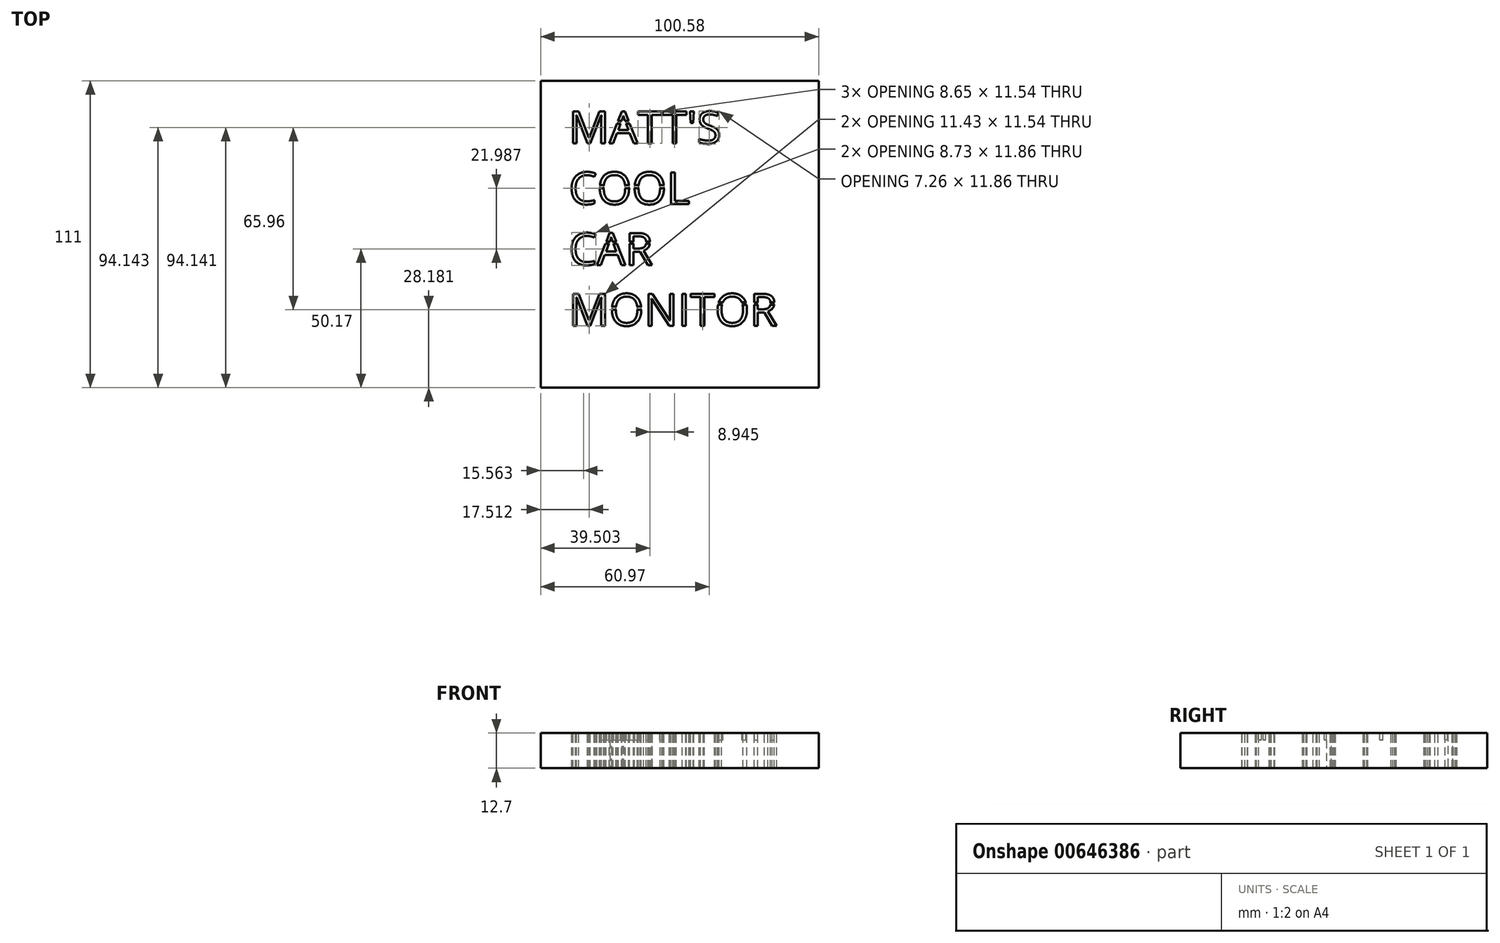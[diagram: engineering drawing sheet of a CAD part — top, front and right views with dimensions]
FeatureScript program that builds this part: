
annotation { "Feature Type Name" : "Feature", "Feature Type Description" : "" }
export const myFeature = defineFeature(function(context is Context, id is Id, definition is map)
    precondition{}
    {
        {
            var Q0;
            Q0=qCreatedBy(makeId("Top.planeOp"),FACE);
            var sketch = newSketch(context, id + "F0", { "sketchPlane" : qUnion([Q0])});
            skLineSegment(sketch, "E0.bottom", {"start": v(-50.3, 59.69) * mm, "end": v(50.3, 59.7) * mm});
            skLineSegment(sketch, "E0.top", {"start": v(-50.3, -51.3) * mm, "end": v(50.3, -51.3) * mm});
            skLineSegment(sketch, "E0.left", {"start": v(-50.3, 59.69) * mm, "end": v(-50.3, -51.3) * mm});
            skLineSegment(sketch, "E0.right", {"start": v(50.3, 59.7) * mm, "end": v(50.3, -51.3) * mm});
            skSolve(sketch);
        }
        {
            var Q0;
            Q0=makeQuery(id+"F0.imprint","IMPRINT",FACE,{"disambiguationData":[TD([[makeQuery(id+"F0.imprint","IMPRINT",EDGE,{"derivedFrom":sQuery(id+"F0.wireOp",EDGE,"E0.bottom")}),-1.0]])]});
            extrude(context, id + "F1", {"entities" : qUnion([Q0]), "depth" : 12.7 * mm, "offsetDistance" : 25.4 * mm});
        }
        {
            var Q0;
            Q0=makeQuery(id+"F1.opExtrude","CAP_FACE",FACE,{"disambiguationData":[OSD([sQuery(id+"F0.wireOp",EDGE,"E0.bottom"),sQuery(id+"F0.wireOp",EDGE,"E0.top"),sQuery(id+"F0.wireOp",EDGE,"E0.left"),sQuery(id+"F0.wireOp",EDGE,"E0.right")])],"isStart":true});
            var sketch = newSketch(context, id + "F2", { "sketchPlane" : qUnion([Q0])});
            skLineSegment(sketch, "E1.bottom", {"start": v(-55.88, 65.31) * mm, "end": v(55.88, 65.31) * mm});
            skLineSegment(sketch, "E1.top", {"start": v(-55.88, -66.22) * mm, "end": v(55.88, -66.22) * mm});
            skLineSegment(sketch, "E1.left", {"start": v(-55.88, 65.31) * mm, "end": v(-55.88, -66.22) * mm});
            skLineSegment(sketch, "E1.right", {"start": v(55.88, 65.31) * mm, "end": v(55.88, -66.22) * mm});
            skSolve(sketch);
        }
        {
            var Q0;
            {var subQ0=sQuery(id+"F2.wireOp",EDGE,"E1.bottom");Q0=makeQuery(id+"F2.imprint","IMPRINT",FACE,{"disambiguationData":[TD([[makeQuery(id+"F2.imprint","IMPRINT",EDGE,{"derivedFrom":subQ0}),-1.0]])]});}
            var Q1;
            {var subQ0=sQuery(id+"F2.wireOp",EDGE,"E1.left");var subQ1=makeQuery(id+"F1.opExtrude","CAP_EDGE",EDGE,{"disambiguationData":[OSD([sQuery(id+"F0.wireOp",EDGE,"E0.top")])],"isStart":true});var subQ2=makeQuery(id+"F2.imprint","INTERSECT",VERTEX,{"derivedFrom":[subQ1,subQ0]});Q1=makeQuery(id+"F2.imprint","IMPRINT",FACE,{"disambiguationData":[TD([[makeQuery(id+"F2.imprint","IMPRINT",EDGE,{"disambiguationData":[TD([[subQ2,-1.0]])],"derivedFrom":subQ0}),1.0]])]});}
            extrude(context, id + "F3", {"entities" : qUnion([Q0, Q1]), "operationType" : NewBodyOperationType.REMOVE, "oppositeDirection" : true, "depth" : 10.16 * mm, "offsetDistance" : 25.4 * mm});
        }
        {
            var Q0;
            Q0=makeQuery(id+"F1.opExtrude","CAP_FACE",FACE,{"disambiguationData":[OSD([sQuery(id+"F0.wireOp",EDGE,"E0.bottom"),sQuery(id+"F0.wireOp",EDGE,"E0.top"),sQuery(id+"F0.wireOp",EDGE,"E0.left"),sQuery(id+"F0.wireOp",EDGE,"E0.right")])],"isStart":false});
            var sketch = newSketch(context, id + "F4", { "sketchPlane" : qUnion([Q0])});
            skText(sketch, "E2", { "text": "MATT\'S\nCOOL\nCAR\nMONITOR", "fontName": "OpenSans-Regular.ttf"});
            const initialGuessF4  = {"E2": [-0.04008, 0.03706, 1, 0, 0.01164]};
            skSetInitialGuess(sketch, initialGuessF4);
            skSolve(sketch);
        }
        {
            var Q0;
            Q0 = qSketchRegion(id + "F4", true);
            extrude(context, id + "F5", {"entities" : qUnion([Q0]), "operationType" : NewBodyOperationType.REMOVE, "oppositeDirection" : true, "depth" : 25.4 * mm, "offsetDistance" : 25.4 * mm});
        }
        {
            var Q0;
            {var subQ0=sQuery(id+"F0.wireOp",EDGE,"E0.right");var subQ1=sQuery(id+"F0.wireOp",EDGE,"E0.left");var subQ2=sQuery(id+"F0.wireOp",EDGE,"E0.bottom");var subQ3=sQuery(id+"F0.wireOp",EDGE,"E0.top");Q0=makeQuery(id+"F5.boolean.opBoolean","SPLIT",FACE,{"disambiguationData":[TD([makeQuery(id+"F1.opExtrude","SWEPT_FACE",FACE,{"disambiguationData":[OSD([subQ2])]})])],"derivedFrom":makeQuery(id+"F1.opExtrude","CAP_FACE",FACE,{"disambiguationData":[OSD([subQ2,subQ3,subQ1,subQ0])],"isStart":false})});}
            var sketch = newSketch(context, id + "F6", { "sketchPlane" : qUnion([Q0])});
            skLineSegment(sketch, "E3.bottom", {"start": v(-24.68, 45.23) * mm, "end": v(-14.94, 45.23) * mm});
            skLineSegment(sketch, "E3.top", {"start": v(-24.68, 44.22) * mm, "end": v(-14.94, 44.22) * mm});
            skLineSegment(sketch, "E3.left", {"start": v(-24.68, 45.23) * mm, "end": v(-24.68, 44.22) * mm});
            skLineSegment(sketch, "E3.right", {"start": v(-14.94, 45.23) * mm, "end": v(-14.94, 44.22) * mm});
            skLineSegment(sketch, "E4.bottom", {"start": v(-30.11, 21.96) * mm, "end": v(-4.44, 21.96) * mm});
            skLineSegment(sketch, "E4.top", {"start": v(-30.11, 20.88) * mm, "end": v(-4.44, 20.88) * mm});
            skLineSegment(sketch, "E4.left", {"start": v(-30.11, 21.96) * mm, "end": v(-30.11, 20.88) * mm});
            skLineSegment(sketch, "E4.right", {"start": v(-4.44, 21.96) * mm, "end": v(-4.44, 20.88) * mm});
            skLineSegment(sketch, "E5.bottom", {"start": v(-27.5, 1.58) * mm, "end": v(-7.08, 1.58) * mm});
            skLineSegment(sketch, "E5.top", {"start": v(-27.5, 0.8) * mm, "end": v(-7.08, 0.8) * mm});
            skLineSegment(sketch, "E5.left", {"start": v(-27.5, 1.58) * mm, "end": v(-27.5, 0.8) * mm});
            skLineSegment(sketch, "E5.right", {"start": v(-7.08, 1.58) * mm, "end": v(-7.08, 0.8) * mm});
            skLineSegment(sketch, "E6.bottom", {"start": v(-25.58, -21.94) * mm, "end": v(-11.3, -21.94) * mm});
            skLineSegment(sketch, "E6.top", {"start": v(-25.58, -23.14) * mm, "end": v(-11.3, -23.14) * mm});
            skLineSegment(sketch, "E6.left", {"start": v(-25.58, -21.94) * mm, "end": v(-25.58, -23.14) * mm});
            skLineSegment(sketch, "E6.right", {"start": v(-11.3, -21.94) * mm, "end": v(-11.3, -23.14) * mm});
            skLineSegment(sketch, "E7.bottom", {"start": v(12.6, -20.46) * mm, "end": v(38.23, -20.46) * mm});
            skLineSegment(sketch, "E7.top", {"start": v(12.6, -21.3) * mm, "end": v(38.23, -21.3) * mm});
            skLineSegment(sketch, "E7.left", {"start": v(12.6, -20.46) * mm, "end": v(12.6, -21.3) * mm});
            skLineSegment(sketch, "E7.right", {"start": v(38.23, -20.46) * mm, "end": v(38.23, -21.3) * mm});
            skSolve(sketch);
        }
        {
            var Q0;
            Q0 = qSketchRegion(id + "F6", true);
            extrude(context, id + "F7", {"entities" : qUnion([Q0]), "operationType" : NewBodyOperationType.ADD, "oppositeDirection" : true, "depth" : 2.54 * mm, "offsetDistance" : 25.4 * mm});
        }
    });
